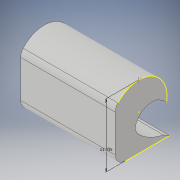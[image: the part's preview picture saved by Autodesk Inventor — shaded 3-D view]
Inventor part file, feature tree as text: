
AUTODESK INVENTOR PART (.ipt)
format: ipt  version: 2019 (Build 230136000, 136)  size: 186,880 bytes
history: native  units: in
note: dims shown in document units (in); Inventor stores cm internally (conversion verified against a paired STEP export)
features: sketch x4, extrude x3, fillet x2, plane x1, mirror x1
ambient origin geometry x8: Origin, YZ Plane, XZ Plane, XY Plane, X Axis, Y Axis, Z Axis, Center Point
bodies: Solid1 (feature_tree)
feature tree (11):
  extrude  "Extrusion1"  Depth=4.0in
  sketch  "Sketch2"  dims[d21=60.0deg d27=1.65in d28=2.075in d29=0.7in]
  plane  "Work Plane1"
  extrude  "Extrusion2"  Depth=1.65in
  fillet  "Fillet3"  Radius=2.075in
  mirror  "Mirror1"
  fillet  "Fillet2"  Radius=0.7in
  extrude  "Extrusion3"  Depth=2.6239in
  sketch  "Sketch4"  dims[d32=2.8265in d33=3.75in d34=2.6257in d35=0.5in d36=3.7835in d38=0.5104in d39=7.0in d40=0.0in d42=0.1in d43=0.0in d47=2.75in d48=0.75in d49=0.8332in d50=1.2853in d51=2.75in d52=0.6642in d53=2.3361in d54=0.75in d55=0.1in d56=0.0in d57=4.6989in]
  sketch  "Sketch1"  dims[d18=4.0in d20=0.5in]
  sketch  "Sketch3"  dims[d30=2.248in d31=2.6239in]
